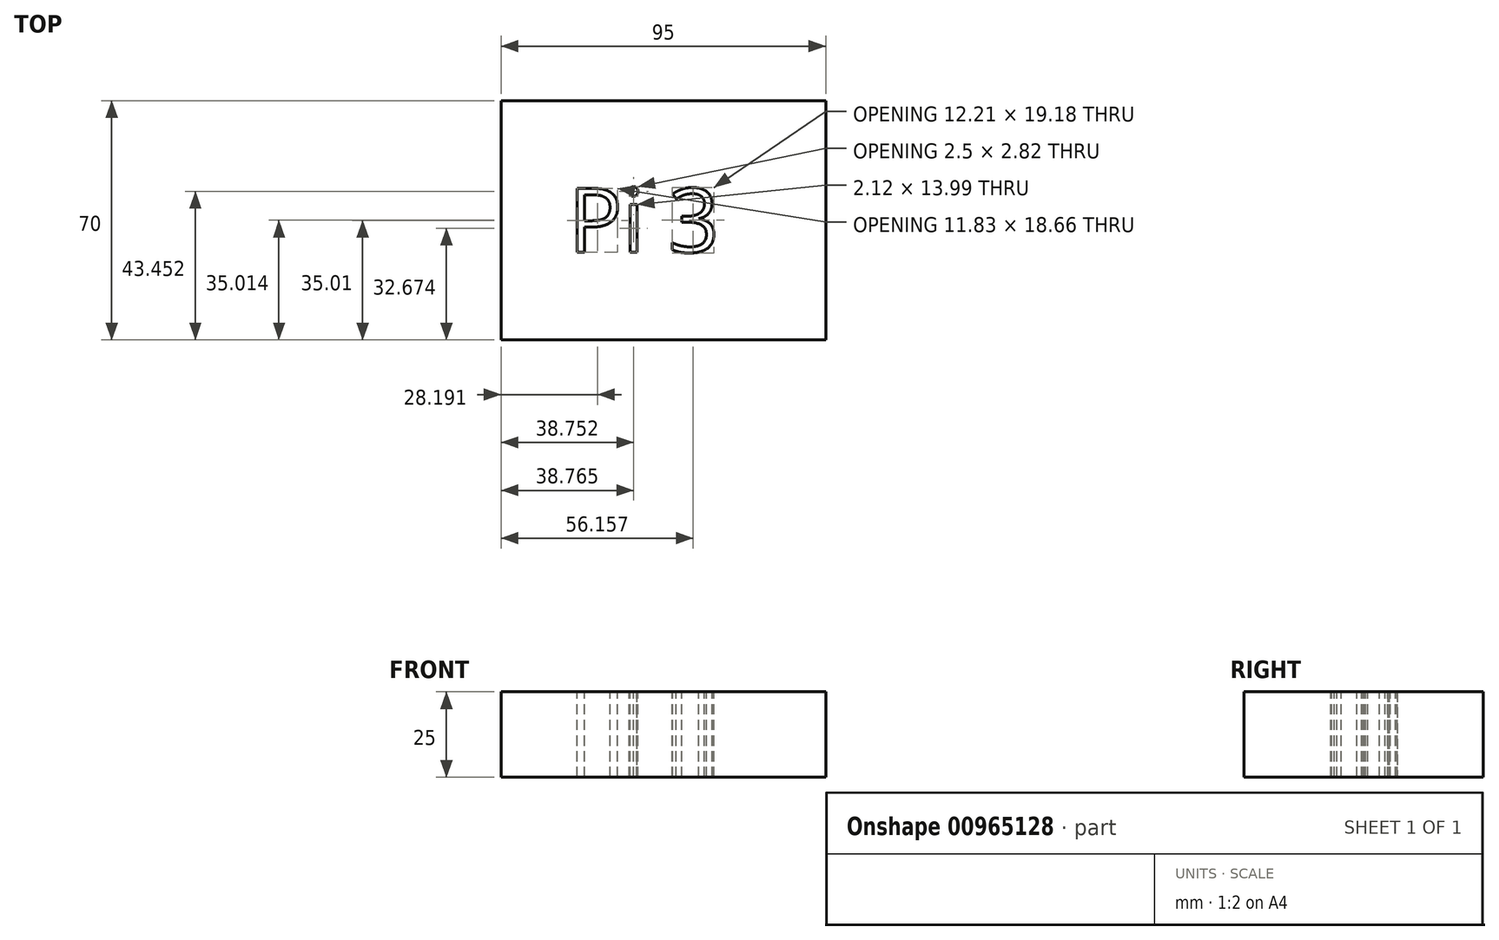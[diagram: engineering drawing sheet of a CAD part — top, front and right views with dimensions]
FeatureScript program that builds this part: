
annotation { "Feature Type Name" : "Feature", "Feature Type Description" : "" }
export const myFeature = defineFeature(function(context is Context, id is Id, definition is map)
    precondition{}
    {
        {
            var Q0;
            Q0=qCreatedBy(makeId("Top.planeOp"),FACE);
            var sketch = newSketch(context, id + "F0", { "sketchPlane" : qUnion([Q0])});
            skLineSegment(sketch, "E0.bottom", {"start": v(-95, 0) * mm, "end": v(0, 0) * mm});
            skLineSegment(sketch, "E0.top", {"start": v(-95, -70) * mm, "end": v(0, -70) * mm});
            skLineSegment(sketch, "E0.left", {"start": v(-95, 0) * mm, "end": v(-95, -70) * mm});
            skLineSegment(sketch, "E0.right", {"start": v(0, 0) * mm, "end": v(0, -70) * mm});
            skSolve(sketch);
        }
        {
            var Q0;
            Q0=makeQuery(id+"F0.imprint","IMPRINT",FACE,{"disambiguationData":[TD([[makeQuery(id+"F0.imprint","IMPRINT",EDGE,{"derivedFrom":sQuery(id+"F0.wireOp",EDGE,"E0.bottom")}),-1.0]])]});
            extrude(context, id + "F1", {"entities" : qUnion([Q0]), "depth" : 25 * mm, "offsetDistance" : 25 * mm});
        }
        {
            var Q0;
            Q0=makeQuery(id+"F1.opExtrude","CAP_FACE",FACE,{"disambiguationData":[OSD([sQuery(id+"F0.wireOp",EDGE,"E0.bottom"),sQuery(id+"F0.wireOp",EDGE,"E0.top"),sQuery(id+"F0.wireOp",EDGE,"E0.left"),sQuery(id+"F0.wireOp",EDGE,"E0.right")])],"isStart":false});
            var sketch = newSketch(context, id + "F2", { "sketchPlane" : qUnion([Q0])});
            skText(sketch, "E1", { "text": "Pi 3", "fontName": "OpenSans-Regular.ttf"});
            const initialGuessF2  = {"E1": [-0.07529, -0.04432, 1, 0, 0.01882]};
            skSetInitialGuess(sketch, initialGuessF2);
            skSolve(sketch);
        }
        {
            var Q0;
            Q0 = qSketchRegion(id + "F2", true);
            extrude(context, id + "F3", {"entities" : qUnion([Q0]), "operationType" : NewBodyOperationType.REMOVE, "oppositeDirection" : true, "depth" : 25 * mm, "offsetDistance" : 25 * mm});
        }
    });
